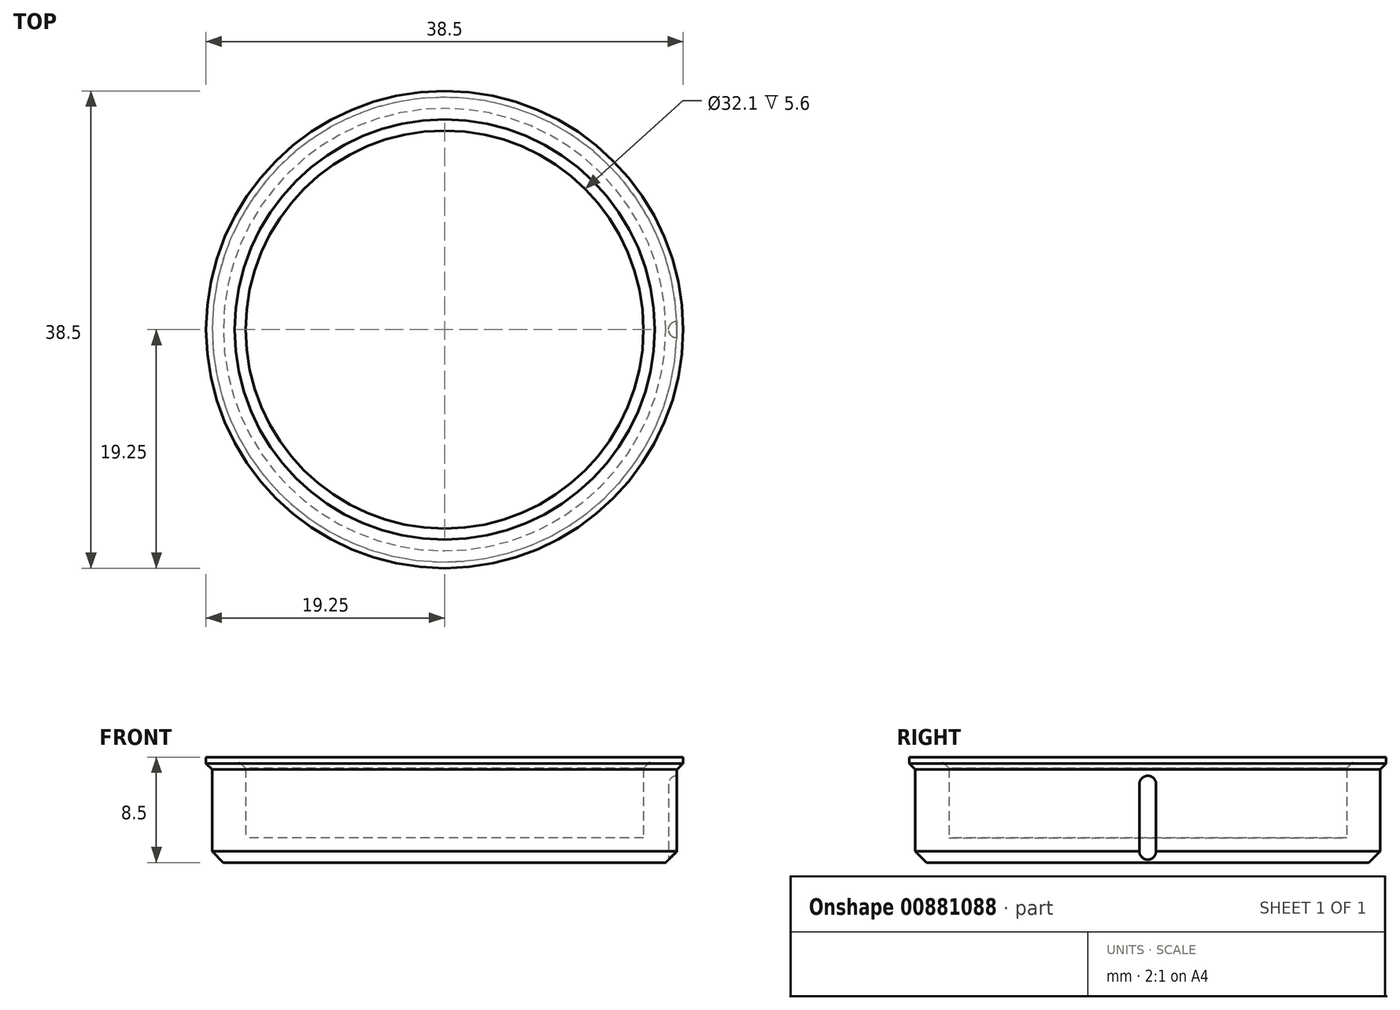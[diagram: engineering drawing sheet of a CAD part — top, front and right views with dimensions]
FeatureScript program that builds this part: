
annotation { "Feature Type Name" : "Feature", "Feature Type Description" : "" }
export const myFeature = defineFeature(function(context is Context, id is Id, definition is map)
    precondition{}
    {
        {
            assignVariable(context, id + "F0", {"name" : "s", "anyValue" : .45});
        }
        {
            var Q0;
            Q0=qCreatedBy(makeId("Top.planeOp"),FACE);
            var sketch = newSketch(context, id + "F1", { "sketchPlane" : qUnion([Q0])});
            skCircle(sketch, "E0", {"center": v(0, 0) * mm, "radius": 16.05 * mm});
            skCircle(sketch, "E1", {"center": v(0, 0) * mm, "radius": 18.75 * mm});
            skSolve(sketch);
        }
        {
            var Q0;
            Q0 = qSketchRegion(id + "F1", true);
            extrude(context, id + "F2", {"entities" : qUnion([Q0]), "depth" : 8.5 * mm, "offsetDistance" : 25 * mm});
        }
        {
            var Q0;
            Q0=makeQuery(id+"F1.imprint","IMPRINT",FACE,{"disambiguationData":[TD([[makeQuery(id+"F1.imprint","IMPRINT",EDGE,{"derivedFrom":sQuery(id+"F1.wireOp",EDGE,"E0")}),1.0]])]});
            extrude(context, id + "F3", {"entities" : qUnion([Q0]), "operationType" : NewBodyOperationType.ADD, "depth" : 2 * mm, "offsetDistance" : 25 * mm});
        }
        {
            var Q0;
            Q0=makeQuery(id+"F2.opExtrude","CAP_EDGE",EDGE,{"disambiguationData":[OSD([sQuery(id+"F1.wireOp",EDGE,"E1")])],"isStart":true});
            chamfer(context, id + "F4", {"entities" : qUnion([Q0]), "width" : (2 * getVariable(context, 's')) * mm, "tangentPropagation" : true});
        }
        {
            var Q0;
            Q0=qCreatedBy(makeId("Front.planeOp"),FACE);
            var sketch = newSketch(context, id + "F5", { "sketchPlane" : qUnion([Q0])});
            skLineSegment(sketch, "E2", {"start": v(18.08, 0) * mm, "end": v(18.08, 6.33) * mm});
            skLineSegment(sketch, "E3", {"start": v(18.75, 8.5) * mm, "end": v(18.75, 7) * mm, "construction": true});
            skArc(sketch, "E4", {"start": v(18.75, 7) * mm, "mid": v(18.27, 6.8) * mm, "end": v(18.08, 6.33) * mm});
            skLineSegment(sketch, "E5", {"start": v(18.75, 7) * mm, "end": v(20, 7) * mm, "construction": true});
            skLineSegment(sketch, "E6", {"start": v(18.08, 0) * mm, "end": v(18.75, 0) * mm});
            skPoint(sketch, "E7", {"position": v(18.75, 7) * mm});
            skLineSegment(sketch, "E8", {"start": v(18.75, 7) * mm, "end": v(18.75, 0) * mm});
            skSolve(sketch);
        }
        {
            var Q0;
            Q0 = qSketchRegion(id + "F5", true);
            var Q1;
            Q1=sQuery(id+"F5.wireOp",EDGE,"E8");
            revolve(context, id + "F6", {"operationType" : NewBodyOperationType.REMOVE, "surfaceOperationType" : NewSurfaceOperationType.NEW, "entities" : qUnion([Q0]), "axis" : qUnion([Q1]), "revolveType" : RevolveType.FULL, "oppositeDirection" : true});
        }
        {
            var Q0;
            Q0=qCreatedBy(makeId("Front.planeOp"),FACE);
            var sketch = newSketch(context, id + "F7", { "sketchPlane" : qUnion([Q0])});
            skPoint(sketch, "E9.0", {"position": v(18.75, 7) * mm});
            skLineSegment(sketch, "E10", {"start": v(18.75, 8.5) * mm, "end": v(18.75, 6.85) * mm});
            skLineSegment(sketch, "E11", {"start": v(18.75, 8.5) * mm, "end": v(19.25, 8.5) * mm});
            skLineSegment(sketch, "E12", {"start": v(19.25, 8.5) * mm, "end": v(19.25, 8) * mm});
            skLineSegment(sketch, "E13", {"start": v(19.25, 8) * mm, "end": v(18.75, 7.5) * mm});
            skSolve(sketch);
        }
        {
            var Q0;
            Q0 = qSketchRegion(id + "F7", true);
            var Q1;
            Q1=makeQuery(id+"F2.opExtrude","CAP_EDGE",EDGE,{"disambiguationData":[OSD([sQuery(id+"F1.wireOp",EDGE,"E1")])],"isStart":false});
            revolve(context, id + "F8", {"operationType" : NewBodyOperationType.ADD, "surfaceOperationType" : NewSurfaceOperationType.NEW, "entities" : qUnion([Q0]), "axis" : qUnion([Q1]), "revolveType" : RevolveType.FULL});
        }
        {
            var Q0;
            Q0=makeQuery(id+"F2.opExtrude","CAP_EDGE",EDGE,{"disambiguationData":[OSD([sQuery(id+"F1.wireOp",EDGE,"E0")])],"isStart":false});
            chamfer(context, id + "F9", {"entities" : qUnion([Q0]), "width" : (2 * getVariable(context, 's')) * mm, "tangentPropagation" : true});
        }
    });
